# Revit family: DL-02 СUBE
name_source: partatom
category: Осветительные приборы
revit_build: Autodesk Revit 2016 (Build: 20151007_0715(x64)
units: mm (PartAtom-declared; Revit-internal decimal feet)

## family parameters
Источник света = Да
Общий = Нет
Основа = Грань
При загрузке вырезать с полостями = Да
Размер круглого соединителя = Использовать диаметр
Тип детали = Нормальный
Точка расчета площади = Нет

## types (6) — shared parameters
ADSK_Единица измерения = Шт.
ADSK_Завод-изготовитель = ГК «Вартон»
ADSK_Количество фаз = 1
ADSK_Количество фаз числовое = 1
ADSK_Коэффициент мощности = 0.9
ADSK_Масса = 0.8
ADSK_Напряжение = 220 В
ADSK_Номинальная мощность = 0 кВт
ADSK_Полная мощность = 0 кВ·А
ADSK_Ток = 0 А
ADSK_Энергоэффективность = 0 лм/Вт
IP Class = IP20
URL = http://varton.ru
Блок аварийного питания = Нет
Видимая форма излучения при визуализации = Нет
Группа модели = Светильники
Изготовитель = ГК «Вартон»
Класс Защиты = I
Класс пожароопасности = нет
Климатическая зона = УХЛ4
Корпус = ABS-пластик
Область использования = Рекомендован для освещения административных и торговых помещений
Плафон = Плафон самосвечение
Полная установленная мощность = 0 кВ·А
Разработчик = ООО ПРОРУБИМ
Разработчик (телефон) = +7 (495) 649-85-43
Разработчик модели (URL) = http://prorubim.com
Светофильтр = 16777215
Смещение цветовой температуры при затухании лампы = <Нет>
Стекло = Остекление
Тип ИС = LED
Угол наклона = -90.00°
Файл фотометрической сетки = V1-R0-00360-20000-200124035degCube-37189.ies
zero-valued in all types: Отметка по умолчанию

## per-type parameters (varying)
| type | ADSK_Наименование | ADSK_Размер_Высота | ADSK_Размер_Длина | ADSK_Размер_Ширина | Излучение по длине прямоугольника | Излучение по ширине прямоугольника | Описание | Тип продукции |
| V1-R0-00360-20000-2001230 | Светильник LED ВАРТОН Downlight квадратный накладной  100 x 100 x 110 мм 12Вт 3000К 35° | 110 мм | 100 мм | 100 мм | 100 мм | 100 мм | Светильник LED ВАРТОН Downlight квадратный накладной  100 x 100 x 110 мм 12Вт 3000К 35° | Светильник LED ВАРТОН Downlight квадратный накладной  100 x 100 x 110 мм 12Вт 3000К 35° |
| V1-R0-00360-20000-2001240 | Светильник LED ВАРТОН Downlight квадратный накладной  100 x 100 x 110 мм 12Вт 4000К 35° | 110 мм | 100 мм | 100 мм | 100 мм | 100 мм | Светильник LED ВАРТОН Downlight квадратный накладной  100 x 100 x 110 мм 12Вт 4000К 35° | Светильник LED ВАРТОН Downlight квадратный накладной  100 x 100 x 110 мм 12Вт 4000К 35° |
| V1-R0-00360-20000-2002030 | Светильник LED ВАРТОН Downlight квадратный накладной  125 x 125 x 135 мм 20Вт 3000К 35° | 135 мм | 125 мм | 125 мм | 125 мм | 125 мм | Светильник LED ВАРТОН Downlight квадратный накладной  125 x 125 x 135 мм 20Вт 3000К 35° | Светильник LED ВАРТОН Downlight квадратный накладной  125 x 125 x 135 мм 20Вт 3000К 35° |
| V1-R0-00360-20000-2002040 | Светильник LED ВАРТОН Downlight квадратный накладной  125 x 125 x 135 мм 20Вт 4000К 35° | 135 мм | 125 мм | 125 мм | 125 мм | 125 мм | Светильник LED ВАРТОН Downlight квадратный накладной  125 x 125 x 135 мм 20Вт 4000К 35° | Светильник LED ВАРТОН Downlight квадратный накладной  125 x 125 x 135 мм 20Вт 4000К 35° |
| V1-R0-00360-20000-2003630 | Светильник LED ВАРТОН Downlight квадратный накладной  150 x 150 x 160 мм 36Вт 3000К 35° | 160 мм | 150 мм | 150 мм | 150 мм | 150 мм | Светильник LED ВАРТОН Downlight квадратный накладной  150 x 150 x 160 мм 36Вт 3000К 35° | Светильник LED ВАРТОН Downlight квадратный накладной  150 x 150 x 160 мм 36Вт 3000К 35° |
| V1-R0-00360-20000-2003640 | Светильник LED ВАРТОН Downlight квадратный накладной  150 x 150 x 160 мм 36Вт 4000К 35° | 160 мм | 150 мм | 150 мм | 150 мм | 150 мм | Светильник LED ВАРТОН Downlight квадратный накладной  150 x 150 x 160 мм 36Вт 4000К 35° | Светильник LED ВАРТОН Downlight квадратный накладной  150 x 150 x 160 мм 36Вт 4000К 35° |

note: column(s) folded — value = type name in every type: ADSK_Код изделия

## geometry (parser evidence)
native form markers: Blend x2
no freeform markers — native parametric forms only
